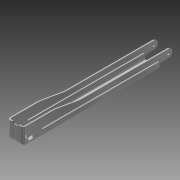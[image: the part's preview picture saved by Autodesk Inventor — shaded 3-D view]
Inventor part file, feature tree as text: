
AUTODESK INVENTOR PART (.ipt)
format: ipt  version: 2011 (Build 150239000, 239)  size: 1,097,728 bytes
history: native  units: mm (DEFAULTED — no unit token found)
features: sketch x14, other x14, sheet_metal_op x13, mirror x3, chamfer x1, emboss x1
ambient origin geometry x8: Origin, YZ Plane, XZ Plane, XY Plane, X Axis, Y Axis, Z Axis, Center Point
bodies: Solid1 (feature_tree)
feature tree (46):
  sheet_metal_op  "Face1"
  sheet_metal_op  "Flange1"
  sheet_metal_op  "Flange2"
  sheet_metal_op  "Flange3"
  sheet_metal_op  "Flange4"
  mirror  "Mirror1"
  sheet_metal_op  "Face2"
  sheet_metal_op  "Face3"
  chamfer  "Corner Round2"
  mirror  "Mirror2"
  emboss  "Emboss1"
  mirror  "Mirror3"
  sketch  "Sketch2"  dims[d0=15.5448mm]
  other  "Plate1"
  sketch  "Sketch3"  dims[d1=133.35mm]
  other  "Plate2"
  sheet_metal_op  "Bend1"
  sketch  "Sketch4"  dims[d2=1.143mm]
  other  "Plate3"
  sheet_metal_op  "Bend2"
  sketch  "Sketch5"  dims[d3=1.143mm]
  other  "Plate4"
  sheet_metal_op  "Bend3"
  sketch  "Sketch6"  dims[d4=0.5715mm]
  other  "Plate5"
  sheet_metal_op  "Bend4"
  sketch  "Sketch7"  dims[d5=2.286mm]
  sketch  "Sketch8"  dims[d6=1.143mm]
  sketch  "Sketch9"  dims[d7=15.875mm d8=90.0deg d9=1.143mm]
  other  "Plate6"
  sheet_metal_op  "Bend5"
  sketch  "Sketch10"  dims[d10=1.143mm]
  other  "Plate7"
  sheet_metal_op  "Bend6"
  sketch  "Sketch11"  dims[d11=0.5715mm]
  sketch  "Sketch12"  dims[d12=2.286mm]
  sketch  "Sketch13"  dims[d13=1.143mm]
  sketch  "Sketch14"  dims[d14=15.875mm d15=90.0deg d16=1.143mm]
  sketch  "Sketch15"  dims[d17=1.143mm d18=0.5715mm d19=2.286mm d20=1.143mm d21=6.35mm d22=90.0deg d23=1.143mm d24=1.143mm d25=0.5715mm d26=2.286mm d27=1.143mm d28=6.35mm d29=90.0deg d30=1.143mm d31=38.1mm d32=12.7mm d33=25.4mm d34=29.670597mm d35=1.143mm d36=0.0mm d37=6.35mm d38=3.175mm d39=1.5748mm d40=1.143mm d41=0.0mm d42=7.9502mm d43=2.3876mm d44=8.7376mm d45=1.143mm d46=1.143mm d47=0.5715mm d48=2.286mm d49=1.143mm d51=1.143mm d52=1.143mm d53=0.5715mm d54=2.286mm d55=1.143mm d56=1.524mm d57=6.35mm d58=1.016mm d59=114.3mm d60=19.05mm d61=1.143mm d62=0.0mm d63=6.35mm d64=3.175mm d65=1.524mm d66=1.143mm d67=0.0mm d68=3.312162mm d69=6.624323mm d70=38.1mm d71=49.500966mm d72=0.127mm d73=0.0mm d74=5.5372mm d75=3.180024mm d76=4.7752mm d77=6.35mm d78=1.143mm d79=0.0mm d80=2.413mm d81=6.35mm d82=3.429mm d83=1.778mm d84=1.143mm d85=0.0mm]
  other  "Cut1"
  other  "Cut2"
  other  "Cut3"
  other  "Cut4"
  other  "Cut5"
  other  "Cut6"
  other  "Definition1"
